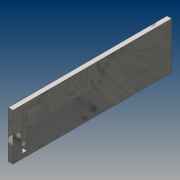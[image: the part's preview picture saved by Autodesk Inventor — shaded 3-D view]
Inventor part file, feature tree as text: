
AUTODESK INVENTOR PART (.ipt)
format: ipt  version: 2021 (Build 250183000, 183)  size: 131,584 bytes
history: native  units: mm
features: extrude x3, sketch x2, mirror x1, chamfer x1, projected_geometry x1
ambient origin geometry x8: Origin, YZ Plane, XZ Plane, XY Plane, X Axis, Y Axis, Z Axis, Center Point
bodies: Solid1 (feature_tree)
feature tree (8):
  extrude  "Extrusion1"  Depth=100.0mm
  sketch  "Sketch2"  dims[d2=10.0mm d3=0.0mm d4=20.0mm d5=10.0mm d6=60.0mm d7=10.0mm d8=0.0mm d9=36.25mm d10=0.0mm d11=16.5mm d12=2.0mm d13=45.0deg]
  extrude  "Extrusion2"  Depth=20.0mm
  extrude  "Extrusion3"  Depth=10.0mm
  mirror  "Mirror1"
  chamfer  "Chamfer1"  Distance=60.0mm
  sketch  "Sketch1"  dims[d0=320.0mm d1=100.0mm]
  projected_geometry  "Projected Loop1"
